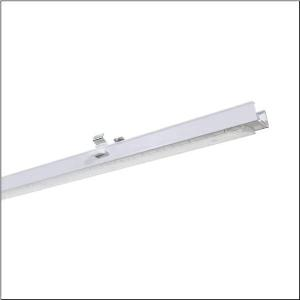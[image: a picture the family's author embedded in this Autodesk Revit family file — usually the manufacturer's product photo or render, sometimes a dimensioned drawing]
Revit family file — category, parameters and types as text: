
# Revit family: trunking_flex_31_51re12ma46b
name_source: partatom
category: Lighting Fixtures
units: mm (PartAtom-declared; Revit-internal decimal feet)

## family parameters
Cut with Voids When Loaded = No
Host = Face
Light Source = No
Part Type = Normal
Room Calculation Point = No
Round Connector Dimension = Use Diameter
Shared = No

## types (1)
- --- (1 x LED, 6400 lm, 40 W, 4000K)
    Apparent Load = 40 VA
    CIE Flux Codes = 65 91 98 99 100
    Color Rendering = 80
    Color Temperature = 4000K
    Default Elevation = 1800 mm
    Description = Trunking Flex 31, luminaire insert, of extruded aluminium section, coated, traffic white (RAL 9016), length: 1.172mm, width: 91mm, height: 53mm, LED rated luminous flux: 6.400lm, light colour: 840, control gear: ON/OFF Multilumen, with system connector: socket, mains connection: 220..240V, AC, 50/60Hz, rated input power: 40W, luminous flux adjustable on luminaire in four steps (3420/4540/5580/6630lm), connected load according to luminous flux setting (20/26/33/40W), primary light control with lens, of plastic, primary optical cover: cover, of PMMA, light emission: direct distribution, protection rating (complete): IP20, insulation class (complete): insulation class I (protective earthing), certification: CE, UKCA, impact resistance: IK02, permissible ambient temperature for indoor applications: -20..+40°C, packaging unit: 1 piece
    Height = 58 mm
    Lamp = 1 x LED
    Lamp Light Flux = 6400 lm
    Lamp Power = 40 W
    Lamp count = 1
    Length = 1172 mm
    Luminous efficacy = 160 lm/W
    Manufacturer = Siteco
    ModVariant = No
    Model = 51RE12MA46B
    Mounting Place = Ceiling
    Mounting Type = Pendant
    Number of Poles = 1
    OnlyDefault = Yes
    Power Factor = 1
    Product Name = Trunking Flex 31
    Product group = luminaire insert
    ProductGroupID = 901
    Protection Class = Protection class I
    Protection Degree = IP 20
    RLX_Detail_Level = 1
    RLX_Emergency_Light_Flux = 0 lm
    RLX_Emergency_Type = 0
    RLX_Emergency_Type_DB = No
    RlxData = <blob elided: 19953 chars, md5=e2f3b765>
    Socket = socket
    Standby Power = 0 W
    System Light Flux = 6400 lm
    System Power = 40 W
    Type Comments = factory setting: luminous flux: 100 % | (ON | ON) | 300 mA
    Type Image = l_1266702.jpg
    URL = http://relux.com
    VarID = @adj_001297
    Voltage = 0 V
    Weight = 0.00 kg
    Width = 65 mm

## geometry (parser evidence)
native form markers: Blend x4, Sweep x11
no freeform markers — native parametric forms only
